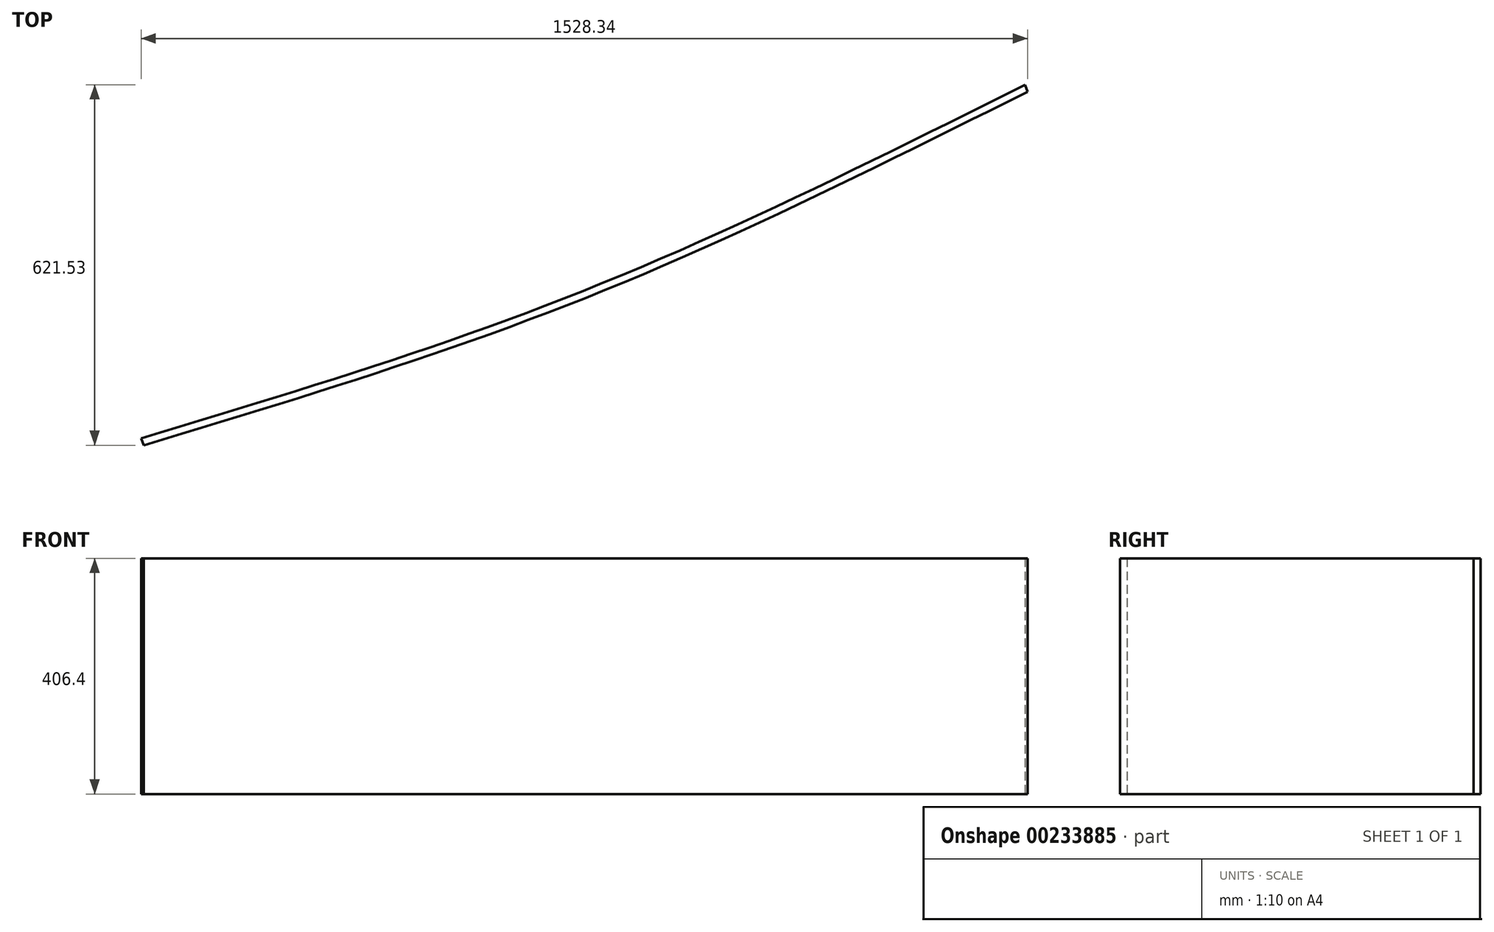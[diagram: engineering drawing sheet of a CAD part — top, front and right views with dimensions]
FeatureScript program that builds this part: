
annotation { "Feature Type Name" : "Feature", "Feature Type Description" : "" }
export const myFeature = defineFeature(function(context is Context, id is Id, definition is map)
    precondition{}
    {
        {
            var Q0;
            Q0=qCreatedBy(makeId("Top.planeOp"),FACE);
            var sketch = newSketch(context, id + "F0", { "sketchPlane" : qUnion([Q0])});
            skLineSegment(sketch, "E0", {"start": v(0, 0) * mm, "end": v(-1524, 0) * mm, "construction": true});
            skLineSegment(sketch, "E1", {"start": v(0, 0) * mm, "end": v(0, 609.6) * mm, "construction": true});
            skLineSegment(sketch, "E2", {"start": v(-762, 0) * mm, "end": v(-762, 254) * mm, "construction": true});
            skFitSpline(sketch, "E3", {"points": [v(-1524, 0) * mm, v(-762, 254) * mm, v(0, 609.6) * mm], "startDerivative": vector(1550.3, 467.12) * mm, "endDerivative": vector(1497.9, 751) * mm});
            skLineSegment(sketch, "E4", {"start": v(-1524, 0) * mm, "end": v(-1528.34, 11.93) * mm});
            skLineSegment(sketch, "E5", {"start": v(-762, 254) * mm, "end": v(-766.34, 265.93) * mm});
            skLineSegment(sketch, "E6", {"start": v(0, 609.6) * mm, "end": v(-4.34, 621.53) * mm});
            skFitSpline(sketch, "E7", {"points": [v(-1528.34, 11.93) * mm, v(-766.34, 265.93) * mm, v(-4.34, 621.53) * mm], "startDerivative": vector(1550.3, 467.12) * mm, "endDerivative": vector(1497.9, 751) * mm});
            skSolve(sketch);
        }
        {
            var Q0;
            {var subQ0=sQuery(id+"F0.wireOp",EDGE,"E4");Q0=makeQuery(id+"F0.imprint","IMPRINT",FACE,{"disambiguationData":[TD([[makeQuery(id+"F0.imprint","IMPRINT",EDGE,{"derivedFrom":subQ0}),-1.0]])]});}
            var Q1;
            {var subQ2=sQuery(id+"F0.wireOp",EDGE,"E5");Q1=makeQuery(id+"F0.imprint","IMPRINT",FACE,{"disambiguationData":[TD([[makeQuery(id+"F0.imprint","IMPRINT",EDGE,{"derivedFrom":subQ2}),-1.0]])]});}
            extrude(context, id + "F1", {"entities" : qUnion([Q0, Q1]), "depth" : 406.4 * mm});
        }
    });
